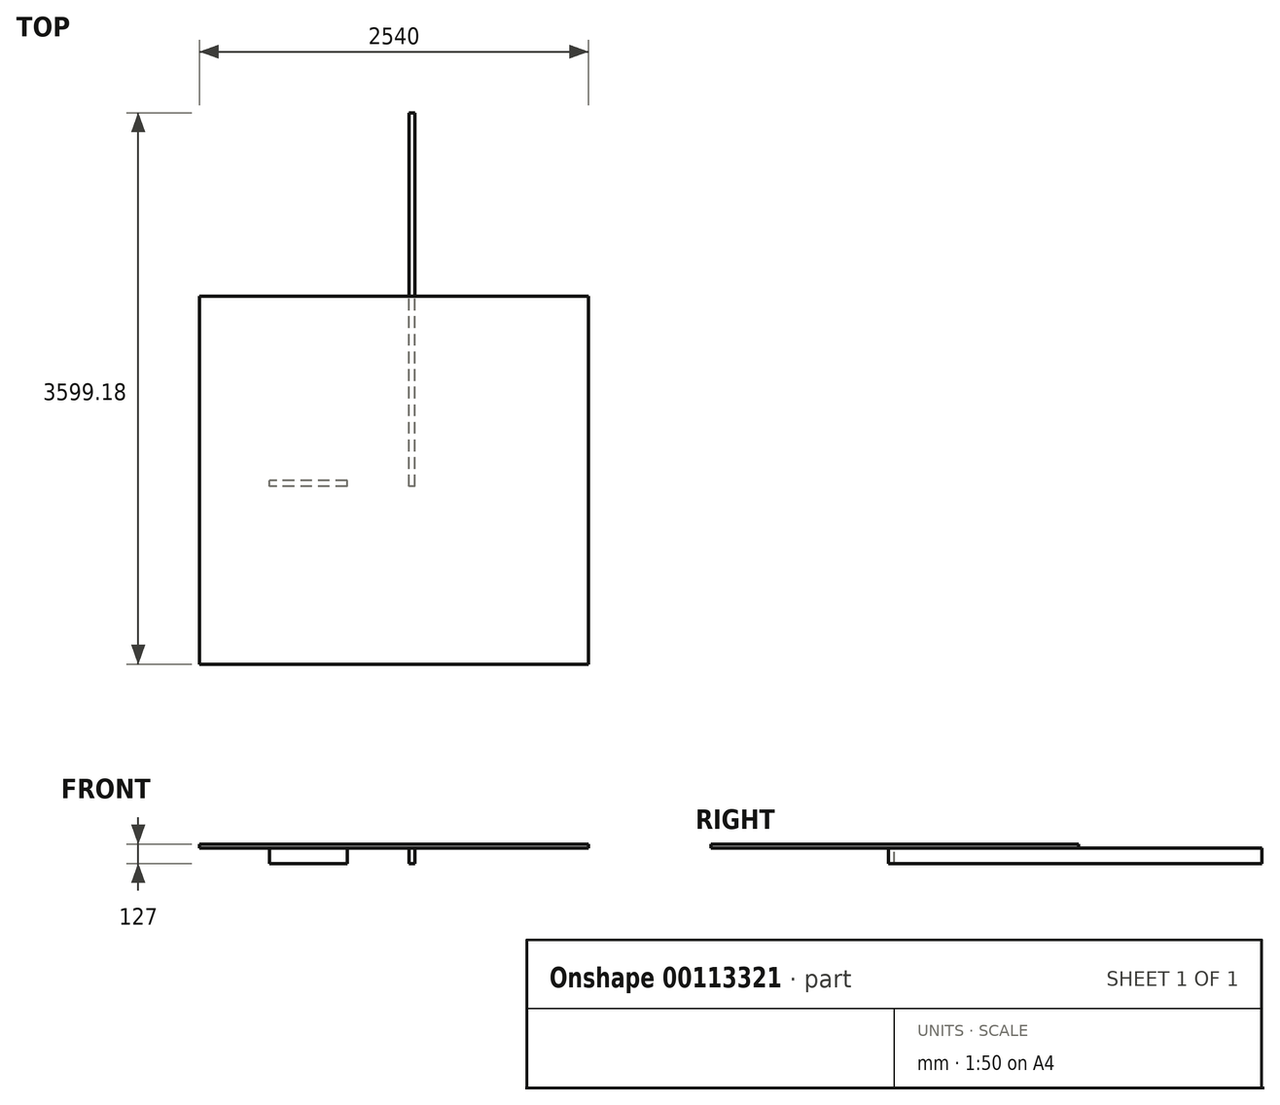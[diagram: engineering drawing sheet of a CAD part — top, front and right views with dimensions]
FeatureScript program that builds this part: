
annotation { "Feature Type Name" : "Feature", "Feature Type Description" : "" }
export const myFeature = defineFeature(function(context is Context, id is Id, definition is map)
    precondition{}
    {
        {
            var Q0;
            Q0=qCreatedBy(makeId("Top.planeOp"),FACE);
            var sketch = newSketch(context, id + "F0", { "sketchPlane" : qUnion([Q0])});
            skLineSegment(sketch, "E0.bottom", {"start": v(71.65, -77.4) * mm, "end": v(33.55, -77.4) * mm});
            skLineSegment(sketch, "E0.top", {"start": v(71.65, 2361) * mm, "end": v(33.55, 2361) * mm});
            skLineSegment(sketch, "E0.left", {"start": v(71.65, -77.4) * mm, "end": v(71.65, 2361) * mm});
            skLineSegment(sketch, "E0.right", {"start": v(33.55, -77.4) * mm, "end": v(33.55, 2361) * mm});
            skSolve(sketch);
        }
        {
            var Q0;
            Q0=makeQuery(id+"F0.imprint","IMPRINT",FACE,{"disambiguationData":[TD([[makeQuery(id+"F0.imprint","IMPRINT",EDGE,{"derivedFrom":sQuery(id+"F0.wireOp",EDGE,"E0.bottom")}),-1.0]])]});
            extrude(context, id + "F1", {"entities" : qUnion([Q0]), "oppositeDirection" : true, "depth" : 101.6 * mm});
        }
        {
            var Q0;
            Q0=qCreatedBy(makeId("Top.planeOp"),FACE);
            var sketch = newSketch(context, id + "F2", { "sketchPlane" : qUnion([Q0])});
            skLineSegment(sketch, "E1.bottom", {"start": v(-370.99, -78.73) * mm, "end": v(-878.99, -78.73) * mm});
            skLineSegment(sketch, "E1.top", {"start": v(-370.99, -40.63) * mm, "end": v(-878.99, -40.63) * mm});
            skLineSegment(sketch, "E1.left", {"start": v(-370.99, -78.73) * mm, "end": v(-370.99, -40.63) * mm});
            skLineSegment(sketch, "E1.right", {"start": v(-878.99, -78.73) * mm, "end": v(-878.99, -40.63) * mm});
            skSolve(sketch);
        }
        {
            var Q0;
            Q0=makeQuery(id+"F2.imprint","IMPRINT",FACE,{"disambiguationData":[TD([[makeQuery(id+"F2.imprint","IMPRINT",EDGE,{"derivedFrom":sQuery(id+"F2.wireOp",EDGE,"E1.bottom")}),-1.0]])]});
            var Q1;
            Q1=sQuery(id+"F2.wireOp",EDGE,"E1.top");
            var Q2;
            Q2=sQuery(id+"F2.wireOp",EDGE,"E1.bottom");
            extrude(context, id + "F3", {"entities" : qUnion([Q0]), "surfaceEntities" : qUnion([Q1, Q2]), "oppositeDirection" : true, "depth" : 101.6 * mm});
        }
        {
            var Q0;
            Q0=qCreatedBy(makeId("Top.planeOp"),FACE);
            var sketch = newSketch(context, id + "F4", { "sketchPlane" : qUnion([Q0])});
            skLineSegment(sketch, "E2.bottom", {"start": v(-1335.56, 1163.96) * mm, "end": v(1204.44, 1163.96) * mm});
            skLineSegment(sketch, "E2.top", {"start": v(-1335.56, -1238.2) * mm, "end": v(1204.44, -1238.2) * mm});
            skLineSegment(sketch, "E2.left", {"start": v(-1335.56, 1163.96) * mm, "end": v(-1335.56, -1238.2) * mm});
            skLineSegment(sketch, "E2.right", {"start": v(1204.44, 1163.96) * mm, "end": v(1204.44, -1238.2) * mm});
            skSolve(sketch);
        }
        {
            var Q0;
            Q0=makeQuery(id+"F4.imprint","IMPRINT",FACE,{"disambiguationData":[TD([[makeQuery(id+"F4.imprint","IMPRINT",EDGE,{"derivedFrom":sQuery(id+"F4.wireOp",EDGE,"E2.bottom")}),-1.0]])]});
            extrude(context, id + "F5", {"entities" : qUnion([Q0]), "depth" : 25.4 * mm});
        }
    });
